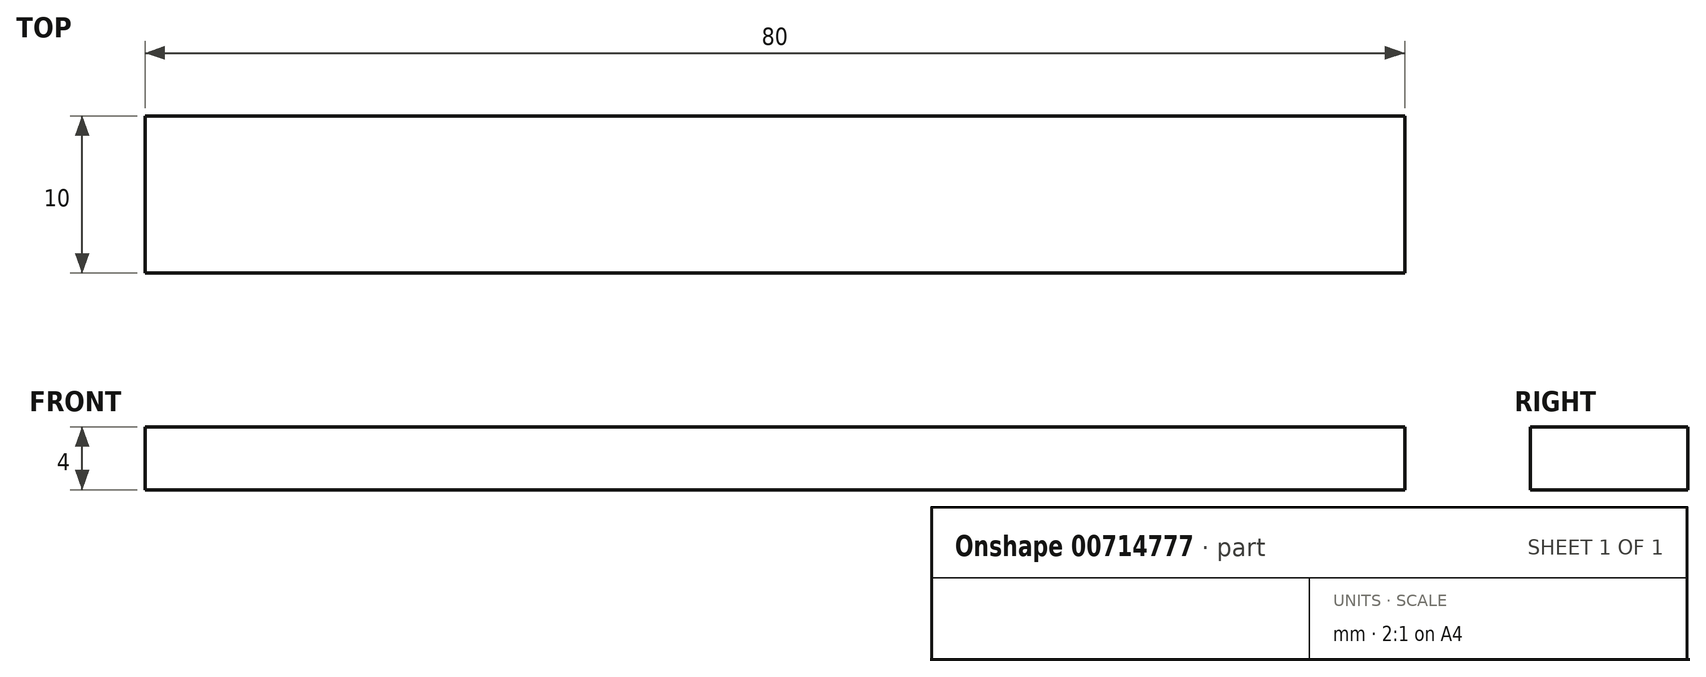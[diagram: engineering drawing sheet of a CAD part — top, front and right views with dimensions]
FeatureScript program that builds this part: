
annotation { "Feature Type Name" : "Feature", "Feature Type Description" : "" }
export const myFeature = defineFeature(function(context is Context, id is Id, definition is map)
    precondition{}
    {
        {
            var Q0;
            Q0=qCreatedBy(makeId("Top.planeOp"),FACE);
            var sketch = newSketch(context, id + "F0", { "sketchPlane" : qUnion([Q0])});
            skLineSegment(sketch, "E0.bottom", {"start": v(0, 0) * mm, "end": v(80, 0) * mm});
            skLineSegment(sketch, "E0.top", {"start": v(0, 10) * mm, "end": v(80, 10) * mm});
            skLineSegment(sketch, "E0.left", {"start": v(0, 0) * mm, "end": v(0, 10) * mm});
            skLineSegment(sketch, "E0.right", {"start": v(80, 0) * mm, "end": v(80, 10) * mm});
            skSolve(sketch);
        }
        {
            var Q0;
            Q0 = qSketchRegion(id + "F0", true);
            extrude(context, id + "F1", {"entities" : qUnion([Q0]), "depth" : 4 * mm, "offsetDistance" : 25 * mm});
        }
    });
